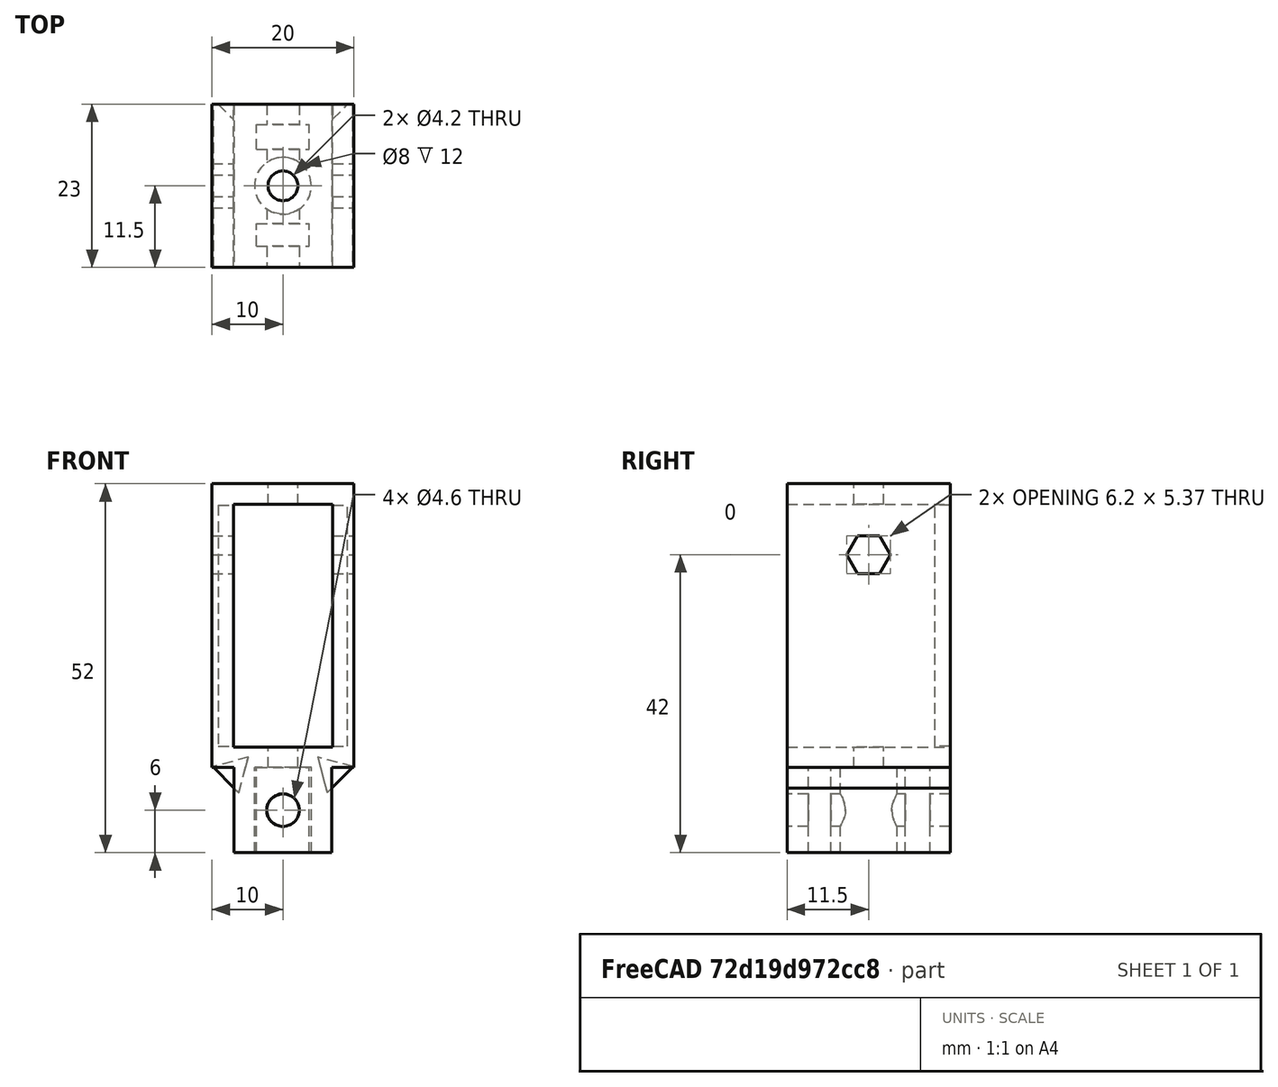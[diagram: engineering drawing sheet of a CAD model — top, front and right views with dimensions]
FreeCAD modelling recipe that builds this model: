
FCSTD DOCUMENT  (FreeCAD 0.19R23634 (Git))
Label: Stage-Side
License: All rights reserved
LicenseURL: http://en.wikipedia.org/wiki/All_rights_reserved
objects: Part::Prism×5, Part::Box×5, Part::Cylinder×3, Part::MultiFuse×2, Part::Cut×1, PartDesign::FeatureBase×1, PartDesign::CoordinateSystem×1, PartDesign::Body×1, App::Part×1
note: 19 computed .brp shape members not serialized (recipe doc carries the construction recipe); baked Part::Feature solids carry a one-line shape summary decoded from their .brp

FEATURE [Part::Prism] prism012
  AttacherType = Attacher::AttachEngine3D
  Circumradius = 3
  FirstAngle = 0
  Height = 34
  Placement = pos=(-7,11.5,49) rot=(0,0,-1;1.309rad)
  Polygon = 3
  SecondAngle = 0
FEATURE [Part::Prism] prism013
  AttacherType = Attacher::AttachEngine3D
  Circumradius = 3.1
  FirstAngle = 0
  Height = 21
  Placement = pos=(-10.5,2e-15,76) rot=(0.57735,0.57735,0.57735;2.0944rad)
  Polygon = 6
  SecondAngle = 0
FEATURE [Part::Cylinder] cylinder010
  Angle = 360
  AttacherType = Attacher::AttachEngine3D
  Height = 43
  Placement = pos=(0,0,44.5) rot=(0,0,1;0rad)
  Radius = 2.1
FEATURE [Part::Box] cube016
  AttacherType = Attacher::AttachEngine3D
  Height = 12
  Length = 13.8
  Placement = pos=(-6.9,-11.5,34) rot=(0,0,1;0rad)
  Width = 23
FEATURE [Part::Cylinder] cylinder011
  Angle = 360
  AttacherType = Attacher::AttachEngine3D
  Height = 12
  Placement = pos=(0,0,34) rot=(0,0,1;0rad)
  Radius = 4
FEATURE [Part::Prism] prism011
  AttacherType = Attacher::AttachEngine3D
  Circumradius = 3
  FirstAngle = 0
  Height = 34
  Placement = pos=(7,11.5,49) rot=(0,0,1;0.261799rad)
  Polygon = 3
  SecondAngle = 0
FEATURE [Part::Box] cube019
  AttacherType = Attacher::AttachEngine3D
  Height = 12
  Length = 7.4
  Placement = pos=(-3.7,5.14,34) rot=(0,0,1;0rad)
  Width = 3.52
FEATURE [Part::Box] cube015
  AttacherType = Attacher::AttachEngine3D
  Height = 40
  Length = 20
  Placement = pos=(-10,-11.5,46) rot=(0,0,1;0rad)
  Width = 23
FEATURE [Part::Box] cube017
  AttacherType = Attacher::AttachEngine3D
  Height = 34.2
  Length = 14
  Placement = pos=(-7,-11.5,48.9) rot=(0,0,1;0rad)
  Width = 23
FEATURE [Part::Prism] prism009
  AttacherType = Attacher::AttachEngine3D
  Circumradius = 3
  FirstAngle = 0
  Height = 23
  Placement = pos=(7,11.5,45.35) rot=(0.983106,-0.129428,0.129428;1.58783rad)
  Polygon = 3
  SecondAngle = 0
FEATURE [Part::Prism] prism010
  AttacherType = Attacher::AttachEngine3D
  Circumradius = 3
  FirstAngle = 0
  Height = 23
  Placement = pos=(-7,11.5,45.35) rot=(-0.092692,0.704063,-0.704063;3.32645rad)
  Polygon = 3
  SecondAngle = 0
FEATURE [Part::MultiFuse] Group006
  Shapes = -> [cube015,cube016,prism009,prism010]
FEATURE [Part::Cylinder] cylinder012
  Angle = 360
  AttacherType = Attacher::AttachEngine3D
  Height = 71
  Placement = pos=(0,35.5,40) rot=(1,0,0;1.5708rad)
  Radius = 2.3
FEATURE [Part::Box] cube018
  AttacherType = Attacher::AttachEngine3D
  Height = 12
  Length = 7.4
  Placement = pos=(-3.7,-8.5,34) rot=(0,0,1;0rad)
  Width = 3.2
FEATURE [Part::MultiFuse] Group007
  Shapes = -> [cube017,cylinder010,cylinder011,cylinder012,cube018,cube019,prism011,prism012,prism013]
FEATURE [Part::Cut] difference004
  Base = -> Group006
  Tool = -> Group007
FEATURE [PartDesign::FeatureBase] BaseFeature004
  BaseFeature = -> difference004
FEATURE [PartDesign::CoordinateSystem] LCS_0  label="Bottom"
  AttacherType = Attacher::AttachEngine3D
  MapMode = 45
  Placement = pos=(-4e-16,-0.0751551,34) rot=(0,0,1;0rad)
  Support = -> [BaseFeature004]
FEATURE [PartDesign::Body] Body004  label="Side Slider"
  BaseFeature = -> difference004
  Group = -> [BaseFeature004]
  Origin = -> Origin004
  Tip = -> BaseFeature004
FEATURE [App::Part] Part  label="SideSlider"
  Group = -> [LCS_0,prism011,cube015,prism010,prism012,cylinder010,prism009,Group006,cylinder012,cube016,prism013,cube017,cube018,Group007,difference004,cube019,cylinder011,Body004]
  Origin = -> Origin
